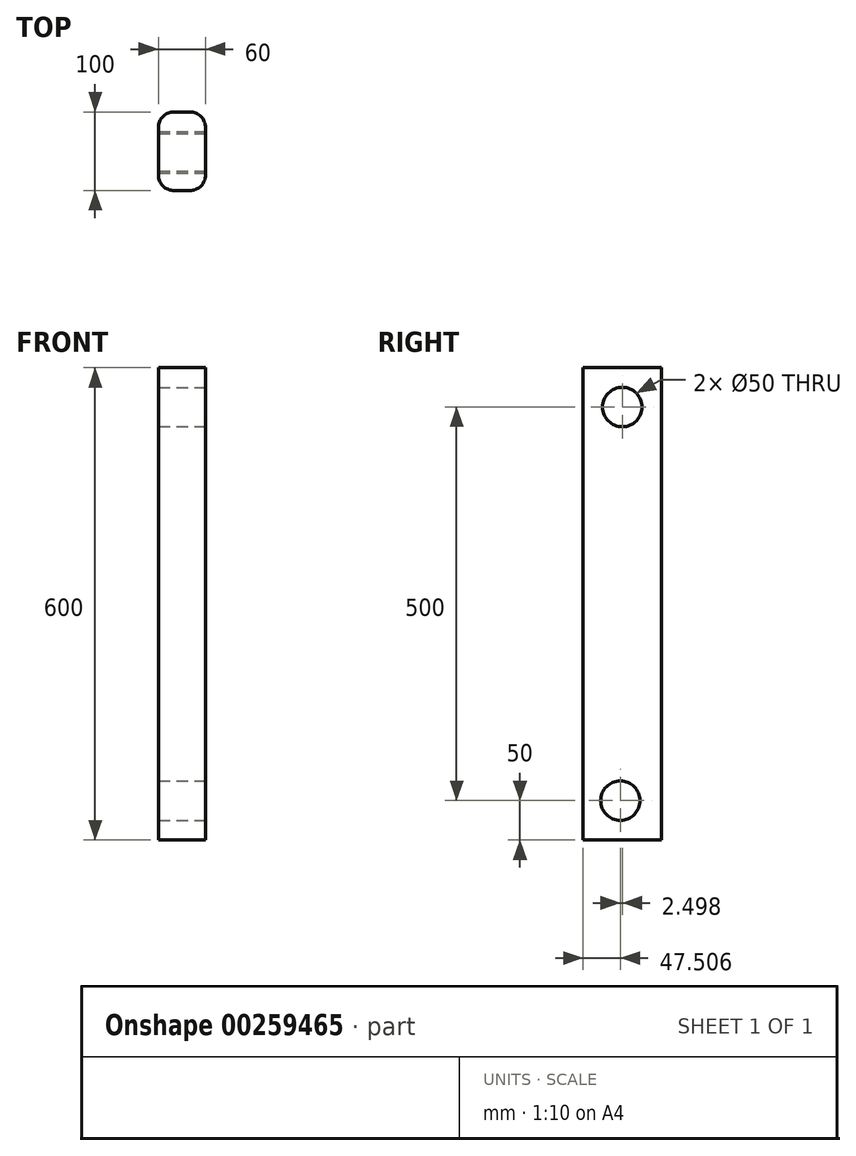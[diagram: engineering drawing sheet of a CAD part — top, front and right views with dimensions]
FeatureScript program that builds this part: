
annotation { "Feature Type Name" : "Feature", "Feature Type Description" : "" }
export const myFeature = defineFeature(function(context is Context, id is Id, definition is map)
    precondition{}
    {
        {
            var Q0;
            Q0=qCreatedBy(makeId("Top.planeOp"),FACE);
            var sketch = newSketch(context, id + "F0", { "sketchPlane" : qUnion([Q0])});
            skLineSegment(sketch, "E0.bottom", {"start": v(-29.26, 77.6) * mm, "end": v(30.74, 77.6) * mm});
            skLineSegment(sketch, "E0.top", {"start": v(-29.26, -22.4) * mm, "end": v(30.74, -22.4) * mm});
            skLineSegment(sketch, "E0.left", {"start": v(-29.26, 77.6) * mm, "end": v(-29.26, -22.4) * mm});
            skLineSegment(sketch, "E0.right", {"start": v(30.74, 77.6) * mm, "end": v(30.74, -22.4) * mm});
            skSolve(sketch);
        }
        {
            var Q0;
            Q0 = qSketchRegion(id + "F0", true);
            extrude(context, id + "F1", {"entities" : qUnion([Q0]), "depth" : 600 * mm});
        }
        {
            var Q0;
            Q0=makeQuery(id+"F1.opExtrude","SWEPT_EDGE",EDGE,{"disambiguationData":[OSD([sQuery(id+"F0.wireOp",EDGE,"E0.top"),sQuery(id+"F0.wireOp",EDGE,"E0.left")])]});
            var Q1;
            Q1=makeQuery(id+"F1.opExtrude","SWEPT_EDGE",EDGE,{"disambiguationData":[OSD([sQuery(id+"F0.wireOp",EDGE,"E0.top"),sQuery(id+"F0.wireOp",EDGE,"E0.right")])]});
            var Q2;
            Q2=makeQuery(id+"F1.opExtrude","SWEPT_EDGE",EDGE,{"disambiguationData":[OSD([sQuery(id+"F0.wireOp",EDGE,"E0.bottom"),sQuery(id+"F0.wireOp",EDGE,"E0.right")])]});
            var Q3;
            Q3=makeQuery(id+"F1.opExtrude","SWEPT_EDGE",EDGE,{"disambiguationData":[OSD([sQuery(id+"F0.wireOp",EDGE,"E0.bottom"),sQuery(id+"F0.wireOp",EDGE,"E0.left")])]});
            fillet(context, id + "F2", {"entities" : qUnion([Q0, Q1, Q2, Q3]), "radius" : 20 * mm, "tangentPropagation" : true, "allowEdgeOverflow" : false});
        }
        {
            var Q0;
            Q0=makeQuery(id+"F1.opExtrude","SWEPT_FACE",FACE,{"disambiguationData":[OSD([sQuery(id+"F0.wireOp",EDGE,"E0.right")])]});
            var sketch = newSketch(context, id + "F3", { "sketchPlane" : qUnion([Q0])});
            skPoint(sketch, "E1", {"position": v(25.1, 50) * mm});
            skPoint(sketch, "E2", {"position": v(27.6, 550) * mm});
            skPoint(sketch, "E2.positionSnap0", {"position": v(27.6, 600) * mm});
            skSolve(sketch);
        }
        {
            var Q0;
            Q0=sQuery(id+"F3.wireOp",VERTEX,"E2");
            var Q1;
            Q1=sQuery(id+"F3.wireOp",VERTEX,"E1");
            var Q2;
            Q2=makeQuery(id+"F1.opExtrude","SWEPT_BODY",BODY,{"disambiguationData":[OSD([sQuery(id+"F0.wireOp",EDGE,"E0.bottom"),sQuery(id+"F0.wireOp",EDGE,"E0.top"),sQuery(id+"F0.wireOp",EDGE,"E0.left"),sQuery(id+"F0.wireOp",EDGE,"E0.right")])]});
            hole(context, id + "F4", {"style" : HoleStyle.SIMPLE, "endStyle" : HoleEndStyle.THROUGH, "holeDiameter" : 50 * mm, "tappedDepth" : 12 * mm, "tapClearance" : 3, "startFromSketch" : true, "locations" : qUnion([Q0, Q1]), "scope" : qUnion([Q2])});
        }
    });
